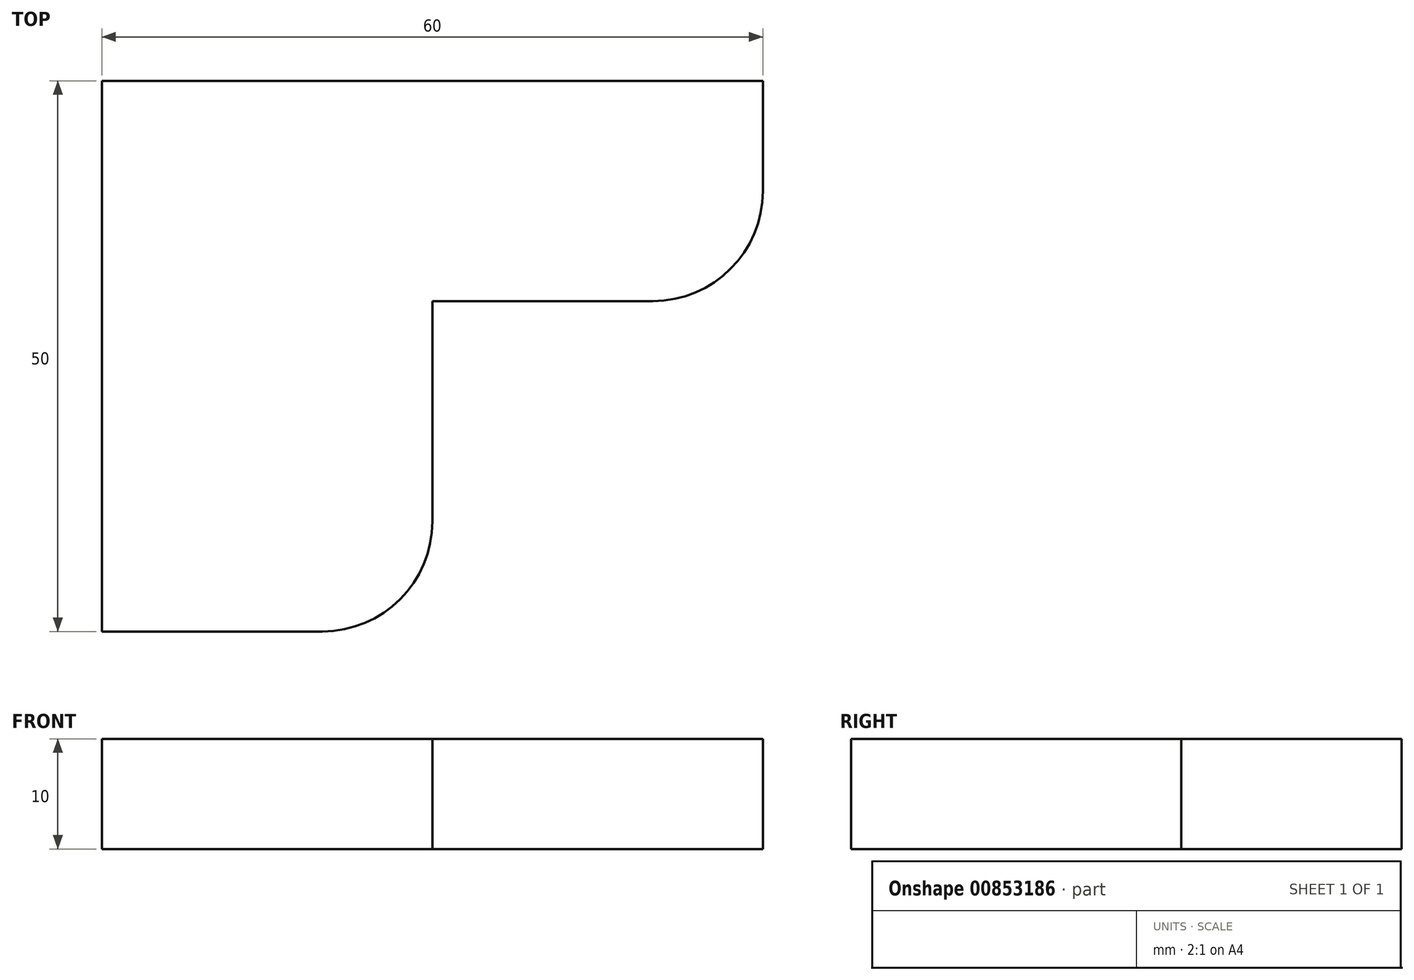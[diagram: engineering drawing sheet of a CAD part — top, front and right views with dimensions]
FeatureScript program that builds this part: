
annotation { "Feature Type Name" : "Feature", "Feature Type Description" : "" }
export const myFeature = defineFeature(function(context is Context, id is Id, definition is map)
    precondition{}
    {
        {
            var Q0;
            Q0=qCreatedBy(makeId("Top.planeOp"),FACE);
            var sketch = newSketch(context, id + "F0", { "sketchPlane" : qUnion([Q0])});
            skLineSegment(sketch, "E0.bottom", {"start": v(-30, 20) * mm, "end": v(0, 20) * mm});
            skLineSegment(sketch, "E0.top", {"start": v(-30, -30) * mm, "end": v(-10, -30) * mm});
            skLineSegment(sketch, "E0.left", {"start": v(-30, 20) * mm, "end": v(-30, -30) * mm});
            skLineSegment(sketch, "E0.right", {"start": v(0, 0) * mm, "end": v(0, -20) * mm});
            skLineSegment(sketch, "E1.bottom", {"start": v(-30, 20) * mm, "end": v(30, 20) * mm});
            skLineSegment(sketch, "E1.top", {"start": v(0, 0) * mm, "end": v(20, 0) * mm});
            skLineSegment(sketch, "E1.left", {"start": v(-30, 20) * mm, "end": v(-30, 0) * mm});
            skLineSegment(sketch, "E1.right", {"start": v(30, 20) * mm, "end": v(30, 10) * mm});
            skPoint(sketch, "E2.visualSharp", {"position": v(30, 0) * mm});
            skArc(sketch, "E2.filletArc", {"start": v(20, 0) * mm, "mid": v(27.07, 2.93) * mm, "end": v(30, 10) * mm});
            skLineSegment(sketch, "E3.bottom", {"start": v(30, 20) * mm, "end": v(20, 20) * mm});
            skLineSegment(sketch, "E3.top", {"start": v(30, 10) * mm, "end": v(20, 10) * mm});
            skLineSegment(sketch, "E3.right", {"start": v(20, 20) * mm, "end": v(20, 10) * mm});
            skLineSegment(sketch, "E4.bottom", {"start": v(20, 10) * mm, "end": v(-10, 10) * mm});
            skLineSegment(sketch, "E4.top", {"start": v(20, 20) * mm, "end": v(-10, 20) * mm});
            skLineSegment(sketch, "E4.left", {"start": v(20, 10) * mm, "end": v(20, 20) * mm});
            skLineSegment(sketch, "E4.right", {"start": v(-10, 10) * mm, "end": v(-10, 20) * mm});
            skPoint(sketch, "E5.visualSharp", {"position": v(0, -30) * mm});
            skArc(sketch, "E5.filletArc", {"start": v(-10, -30) * mm, "mid": v(-2.93, -27.07) * mm, "end": v(0, -20) * mm});
            skLineSegment(sketch, "E6.bottom", {"start": v(-10, 10) * mm, "end": v(-30, 10) * mm});
            skLineSegment(sketch, "E6.top", {"start": v(-10, 20) * mm, "end": v(-30, 20) * mm});
            skLineSegment(sketch, "E6.right", {"start": v(-30, 10) * mm, "end": v(-30, 20) * mm});
            skLineSegment(sketch, "E7.bottom", {"start": v(-30, -30) * mm, "end": v(-20, -30) * mm});
            skLineSegment(sketch, "E7.top", {"start": v(-30, 10) * mm, "end": v(-20, 10) * mm});
            skLineSegment(sketch, "E7.left", {"start": v(-30, -30) * mm, "end": v(-30, 10) * mm});
            skLineSegment(sketch, "E7.right", {"start": v(-20, -30) * mm, "end": v(-20, 10) * mm});
            skSolve(sketch);
        }
        {
            var Q0;
            Q0 = qSketchRegion(id + "F0", true);
            extrude(context, id + "F1", {"entities" : qUnion([Q0]), "depth" : 10 * mm, "offsetDistance" : 25 * mm});
        }
    });
